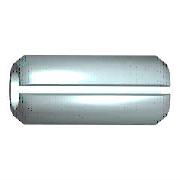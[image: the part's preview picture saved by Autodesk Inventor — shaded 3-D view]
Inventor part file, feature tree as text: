
AUTODESK INVENTOR PART (.ipt)
format: ipt  version: 2016 (Build 200138000, 138)  size: 141,312 bytes
history: native  units: mm (DEFAULTED — no unit token found)
features: sketch x2, other x1, extrude x1
ambient origin geometry x8: Origin, YZ Plane, XZ Plane, XY Plane, X Axis, Y Axis, Z Axis, Center Point
bodies: Solid1 (feature_tree), Body (feature_tree)
feature tree (4):
  other  "IDS_WORKPLANE{1}"
  sketch  "Sketch2"  dims[d2=1.8mm d3=15.0deg d4=15.0deg d10=90.0deg d5=20.0mm d6=0.0mm d7=0.133975mm d8=0.133975mm d9=10.0mm d11=1.5mm d12=0.9mm d14=0.6mm d15=1.256638mm d31=0.0mm d32=0.0mm d33=0.0mm]
  extrude  "Cut"  Depth=20.0mm
  sketch  "Sketch1"  dims[d0=20.0mm d1=3.0mm]
